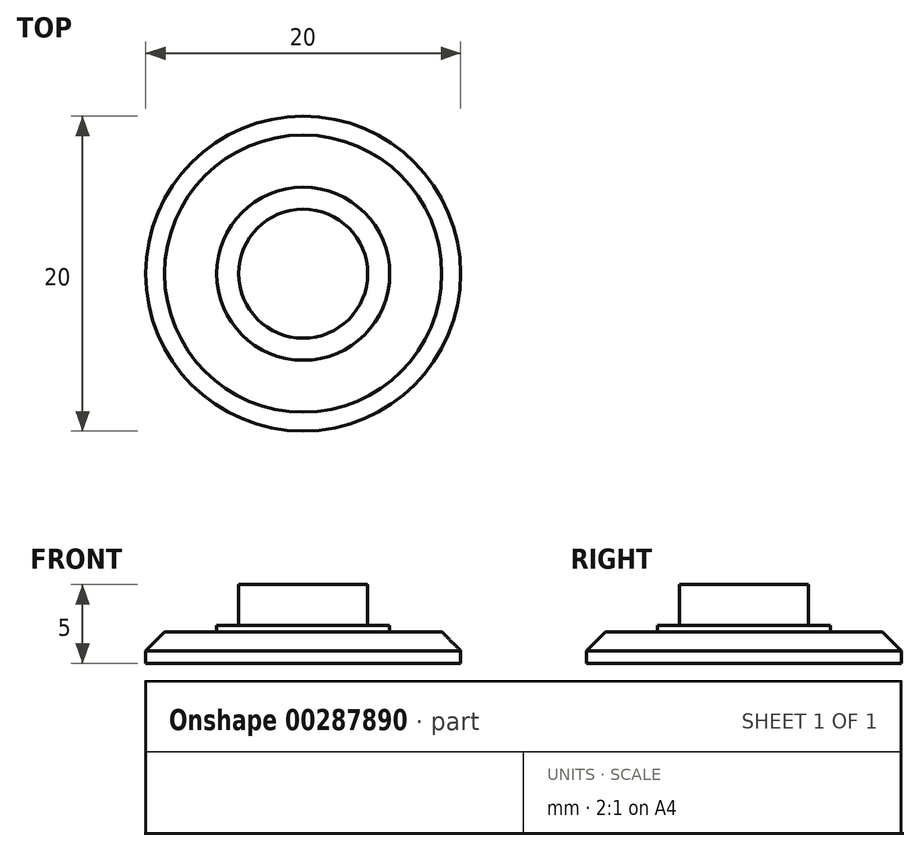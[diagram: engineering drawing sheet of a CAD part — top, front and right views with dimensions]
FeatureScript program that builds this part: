
annotation { "Feature Type Name" : "Feature", "Feature Type Description" : "" }
export const myFeature = defineFeature(function(context is Context, id is Id, definition is map)
    precondition{}
    {
        {
            var Q0;
            Q0=qCreatedBy(makeId("Top.planeOp"),FACE);
            var sketch = newSketch(context, id + "F0", { "sketchPlane" : qUnion([Q0])});
            skCircle(sketch, "E0", {"center": v(0, 0) * mm, "radius": 10 * mm});
            skCircle(sketch, "E1", {"center": v(0, 0) * mm, "radius": 4.1 * mm});
            skCircle(sketch, "E2", {"center": v(0, 0) * mm, "radius": 5.5 * mm});
            skSolve(sketch);
        }
        {
            var Q0;
            Q0=makeQuery(id+"F0.imprint","IMPRINT",FACE,{"disambiguationData":[TD([[makeQuery(id+"F0.imprint","IMPRINT",EDGE,{"derivedFrom":sQuery(id+"F0.wireOp",EDGE,"E0")}),1.0]])]});
            var Q1;
            Q1=makeQuery(id+"F0.imprint","IMPRINT",FACE,{"disambiguationData":[TD([[makeQuery(id+"F0.imprint","IMPRINT",EDGE,{"derivedFrom":sQuery(id+"F0.wireOp",EDGE,"E1")}),1.0]])]});
            var Q2;
            Q2=makeQuery(id+"F0.imprint","IMPRINT",FACE,{"disambiguationData":[TD([[makeQuery(id+"F0.imprint","IMPRINT",EDGE,{"derivedFrom":sQuery(id+"F0.wireOp",EDGE,"E1")}),-1.0]])]});
            extrude(context, id + "F1", {"entities" : qUnion([Q0, Q1, Q2]), "depth" : 2 * mm});
        }
        {
            var Q0;
            Q0=makeQuery(id+"F0.imprint","IMPRINT",FACE,{"disambiguationData":[TD([[makeQuery(id+"F0.imprint","IMPRINT",EDGE,{"derivedFrom":sQuery(id+"F0.wireOp",EDGE,"E1")}),1.0]])]});
            extrude(context, id + "F2", {"entities" : qUnion([Q0]), "operationType" : NewBodyOperationType.ADD, "depth" : 5 * mm});
        }
        {
            var Q0;
            Q0=makeQuery(id+"F1.opExtrude","CAP_EDGE",EDGE,{"disambiguationData":[OSD([sQuery(id+"F0.wireOp",EDGE,"E0")])],"isStart":false});
            chamfer(context, id + "F3", {"entities" : qUnion([Q0]), "width" : 1.2 * mm, "tangentPropagation" : true});
        }
        {
            var Q0;
            Q0=makeQuery(id+"F0.imprint","IMPRINT",FACE,{"disambiguationData":[TD([[makeQuery(id+"F0.imprint","IMPRINT",EDGE,{"derivedFrom":sQuery(id+"F0.wireOp",EDGE,"E1")}),-1.0]])]});
            extrude(context, id + "F4", {"entities" : qUnion([Q0]), "operationType" : NewBodyOperationType.ADD, "depth" : 2.4 * mm});
        }
    });
